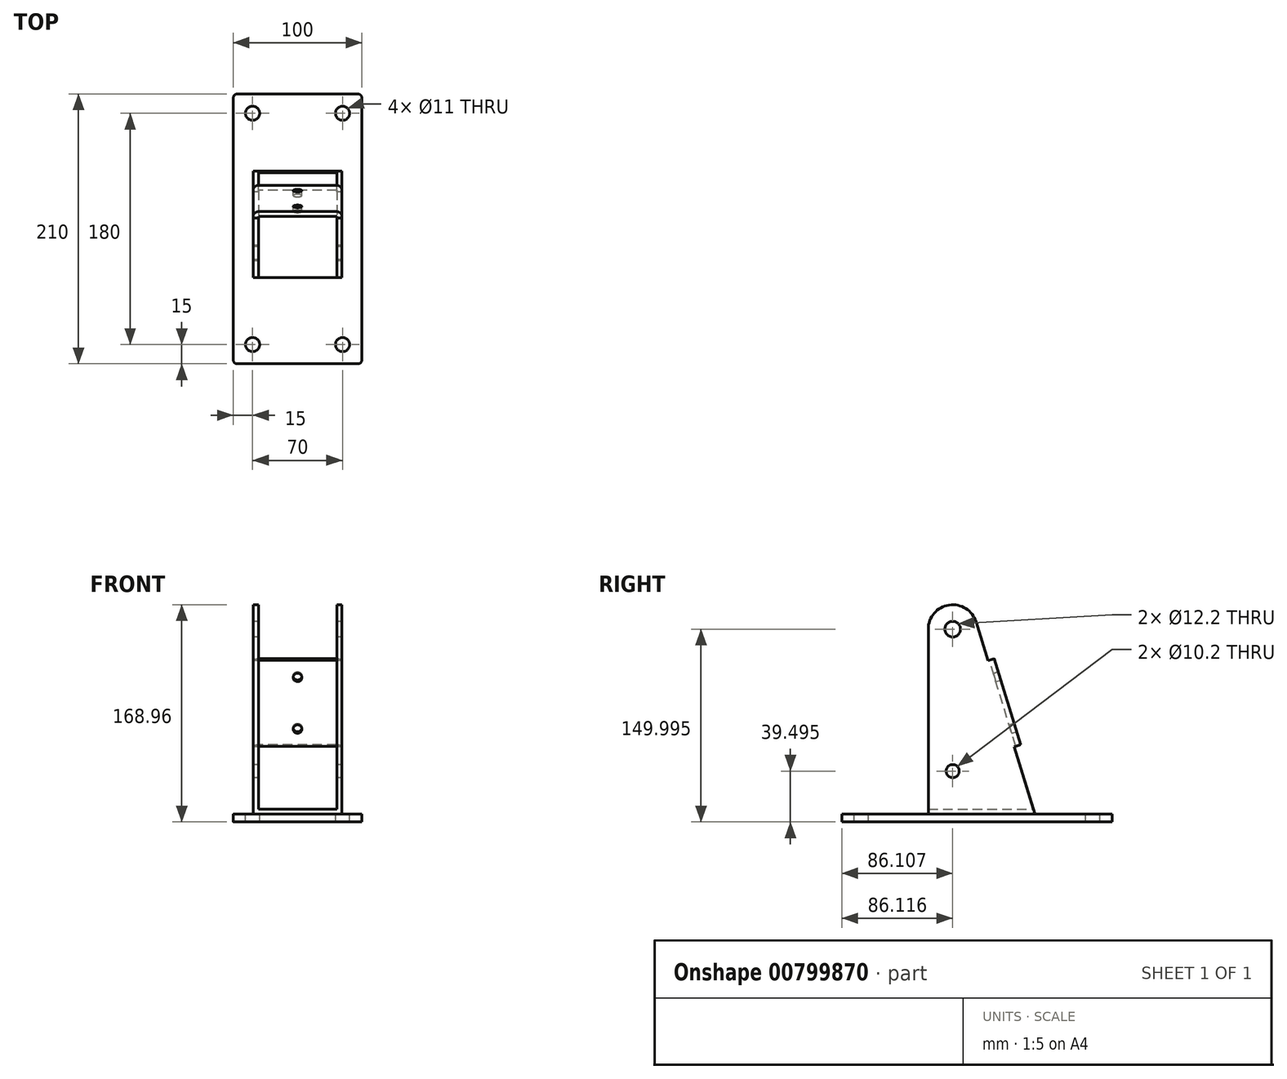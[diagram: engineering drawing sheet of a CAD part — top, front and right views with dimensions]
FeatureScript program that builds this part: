
annotation { "Feature Type Name" : "Feature", "Feature Type Description" : "" }
export const myFeature = defineFeature(function(context is Context, id is Id, definition is map)
    precondition{}
    {
        {
            var Q0;
            Q0=qCreatedBy(makeId("Right.planeOp"),FACE);
            var sketch = newSketch(context, id + "F0", { "sketchPlane" : qUnion([Q0])});
            skLineSegment(sketch, "E0", {"start": v(105, -84.48) * mm, "end": v(-105, -84.48) * mm});
            skLineSegment(sketch, "E1", {"start": v(-105, -84.48) * mm, "end": v(-105, -78.48) * mm});
            skLineSegment(sketch, "E2", {"start": v(-105, -78.48) * mm, "end": v(105, -78.48) * mm});
            skLineSegment(sketch, "E3", {"start": v(105, -78.48) * mm, "end": v(105, -84.48) * mm});
            skLineSegment(sketch, "E4", {"start": v(-37.88, -78.48) * mm, "end": v(45, -78.48) * mm});
            skLineSegment(sketch, "E5", {"start": v(-37.88, 65.48) * mm, "end": v(-37.88, -78.48) * mm});
            skLineSegment(sketch, "E6", {"start": v(28.94, -25.97) * mm, "end": v(45, -78.48) * mm});
            skLineSegment(sketch, "E7", {"start": v(1.89, -78.48) * mm, "end": v(-3.77, -78.48) * mm});
            skCircle(sketch, "E8", {"center": v(-18.88, -44.98) * mm, "radius": 5.1 * mm});
            skCircle(sketch, "E9", {"center": v(-18.9, 65.52) * mm, "radius": 6.1 * mm});
            skArc(sketch, "E10", {"start": v(-0.71, 71.04) * mm, "mid": v(-21.7, 84.28) * mm, "end": v(-37.88, 65.48) * mm});
            skLineSegment(sketch, "E11", {"start": v(-0.71, 71.04) * mm, "end": v(8.48, 40.97) * mm});
            skLineSegment(sketch, "E12", {"start": v(13.45, 42.5) * mm, "end": v(8.48, 40.97) * mm});
            skLineSegment(sketch, "E13", {"start": v(13.45, 42.5) * mm, "end": v(33.92, -24.45) * mm});
            skLineSegment(sketch, "E14", {"start": v(33.92, -24.45) * mm, "end": v(28.94, -25.97) * mm});
            skSolve(sketch);
        }
        {
            var Q0;
            {var subQ1=sQuery(id+"F0.wireOp",EDGE,"E5");Q0=makeQuery(id+"F0.imprint","IMPRINT",FACE,{"disambiguationData":[TD([[makeQuery(id+"F0.imprint","IMPRINT",EDGE,{"derivedFrom":subQ1}),1.0]])]});}
            extrude(context, id + "F1", {"entities" : qUnion([Q0]), "endBound" : BoundingType.SYMMETRIC, "depth" : 69 * mm, "offsetDistance" : 25 * mm});
        }
        {
            var Q0;
            Q0=makeQuery(id+"F1.opExtrude","CAP_EDGE",EDGE,{"disambiguationData":[OSD([sQuery(id+"F0.wireOp",EDGE,"E13")])],"isStart":true});
            var Q1;
            Q1=makeQuery(id+"F1.opExtrude","CAP_EDGE",EDGE,{"disambiguationData":[OSD([sQuery(id+"F0.wireOp",EDGE,"E13")])],"isStart":false});
            fillet(context, id + "F2", {"entities" : qUnion([Q0, Q1]), "radius" : 4 * mm, "tangentPropagation" : true, "allowEdgeOverflow" : false});
        }
        {
            var Q0;
            Q0=makeQuery(id+"F1.opExtrude","SWEPT_FACE",FACE,{"disambiguationData":[OSD([sQuery(id+"F0.wireOp",EDGE,"E5")])]});
            var Q1;
            Q1=makeQuery(id+"F1.opExtrude","SWEPT_FACE",FACE,{"disambiguationData":[OSD([sQuery(id+"F0.wireOp",EDGE,"E10")])]});
            var Q2;
            Q2=makeQuery(id+"F1.opExtrude","SWEPT_FACE",FACE,{"disambiguationData":[OSD([sQuery(id+"F0.wireOp",EDGE,"E11")])]});
            var Q3;
            Q3=makeQuery(id+"F1.opExtrude","SWEPT_FACE",FACE,{"disambiguationData":[OSD([sQuery(id+"F0.wireOp",EDGE,"E6")])]});
            var Q4;
            Q4=makeQuery(id+"F4.opExtrude","SWEPT_FACE",FACE,{"disambiguationData":[OSD([sQuery(id+"F0.wireOp",EDGE,"E0")])]});
            var Q5;
            Q5=makeQuery(id+"F1.opExtrude","SWEPT_FACE",FACE,{"disambiguationData":[OSD([sQuery(id+"F0.wireOp",EDGE,"E12")])]});
            var Q6;
            Q6=makeQuery(id+"F1.opExtrude","SWEPT_FACE",FACE,{"disambiguationData":[OSD([sQuery(id+"F0.wireOp",EDGE,"E14")])]});
            var Q7;
            Q7=makeQuery(id+"F1.opExtrude","SWEPT_FACE",FACE,{"disambiguationData":[OSD([sQuery(id+"F0.wireOp",EDGE,"E4"),sQuery(id+"F0.wireOp",EDGE,"E7")])]});
            var Q8;
            Q8=makeQuery(id+"F1.opExtrude","SWEPT_FACE",FACE,{"disambiguationData":[OSD([sQuery(id+"F0.wireOp",EDGE,"E9")])]});
            var Q9;
            Q9=makeQuery(id+"F1.opExtrude","SWEPT_FACE",FACE,{"disambiguationData":[OSD([sQuery(id+"F0.wireOp",EDGE,"E8")])]});
            shell(context, id + "F3", {"entities" : qUnion([Q0, Q1, Q2, Q3, Q4, Q5, Q6, Q7, Q8, Q9]), "thickness" : 4 * mm});
        }
        {
            var Q0;
            Q0=makeQuery(id+"F0.imprint","IMPRINT",FACE,{"disambiguationData":[TD([[makeQuery(id+"F0.imprint","IMPRINT",EDGE,{"derivedFrom":sQuery(id+"F0.wireOp",EDGE,"E0")}),-1.0]])]});
            extrude(context, id + "F4", {"entities" : qUnion([Q0]), "depth" : 50 * mm, "offsetDistance" : 25 * mm, "hasSecondDirection" : true, "secondDirectionOppositeDirection" : true, "secondDirectionDepth" : 50 * mm});
        }
        {
            var Q0;
            Q0=makeQuery(id+"F4.opExtrude","CAP_EDGE",EDGE,{"disambiguationData":[OSD([sQuery(id+"F0.wireOp",EDGE,"E1")])],"isStart":true});
            var Q1;
            Q1=makeQuery(id+"F4.opExtrude","CAP_EDGE",EDGE,{"disambiguationData":[OSD([sQuery(id+"F0.wireOp",EDGE,"E1")])],"isStart":false});
            var Q2;
            Q2=makeQuery(id+"F4.opExtrude","CAP_EDGE",EDGE,{"disambiguationData":[OSD([sQuery(id+"F0.wireOp",EDGE,"E3")])],"isStart":false});
            var Q3;
            Q3=makeQuery(id+"F4.opExtrude","CAP_EDGE",EDGE,{"disambiguationData":[OSD([sQuery(id+"F0.wireOp",EDGE,"E3")])],"isStart":true});
            fillet(context, id + "F5", {"entities" : qUnion([Q0, Q1, Q2, Q3]), "radius" : 3 * mm, "tangentPropagation" : true, "allowEdgeOverflow" : false});
        }
        {
            var Q0;
            Q0=makeQuery(id+"F4.opExtrude","SWEPT_FACE",FACE,{"disambiguationData":[OSD([sQuery(id+"F0.wireOp",EDGE,"E2"),sQuery(id+"F0.wireOp",EDGE,"E4"),sQuery(id+"F0.wireOp",EDGE,"E7")])]});
            var sketch = newSketch(context, id + "F6", { "sketchPlane" : qUnion([Q0])});
            skPoint(sketch, "E15", {"position": v(-35, -90) * mm});
            skPoint(sketch, "E16.0.1.0", {"position": v(-35, 90) * mm});
            skPoint(sketch, "E16.1.0.0", {"position": v(35, -90) * mm});
            skPoint(sketch, "E16.1.1.0", {"position": v(35, 90) * mm});
            skLineSegment(sketch, "E16.direction1", {"start": v(-35, -90) * mm, "end": v(35, -90) * mm, "construction": true});
            skLineSegment(sketch, "E16.direction2", {"start": v(-35, -90) * mm, "end": v(-35, 90) * mm, "construction": true});
            skSolve(sketch);
        }
        {
            var Q0;
            Q0=sQuery(id+"F6.wireOp",VERTEX,"E16.0.1.0");
            var Q1;
            Q1=sQuery(id+"F6.wireOp",VERTEX,"E15");
            var Q2;
            Q2=sQuery(id+"F6.wireOp",VERTEX,"E16.1.0.0");
            var Q3;
            Q3=sQuery(id+"F6.wireOp",VERTEX,"E16.1.1.0");
            var Q4;
            Q4=makeQuery(id+"F4.opExtrude","SWEPT_BODY",BODY,{"disambiguationData":[OSD([sQuery(id+"F0.wireOp",EDGE,"E0"),sQuery(id+"F0.wireOp",EDGE,"E1"),sQuery(id+"F0.wireOp",EDGE,"E2"),sQuery(id+"F0.wireOp",EDGE,"E3"),sQuery(id+"F0.wireOp",EDGE,"E4"),sQuery(id+"F0.wireOp",EDGE,"E7")])]});
            hole(context, id + "F7", {"style" : HoleStyle.SIMPLE, "endStyle" : HoleEndStyle.THROUGH, "standardTappedOrClearance" : lookupTablePath({ "standard" : "ISO", "size" : "11", "type" : "Drilled" }), "standardBlindInLast" : lookupTablePath({ "standard" : "ISO", "size" : "11", "type" : "Drilled" }), "holeDiameter" : 11 * mm, "majorDiameter" : 5 * mm, "isTappedThrough" : true, "tappedDepth" : 12 * mm, "tapClearance" : 3, "startFromSketch" : true, "locations" : qUnion([Q0, Q1, Q2, Q3]), "scope" : qUnion([Q4])});
        }
        {
            var Q0;
            Q0=makeQuery(id+"F1.opExtrude","SWEPT_FACE",FACE,{"disambiguationData":[OSD([sQuery(id+"F0.wireOp",EDGE,"E13")])]});
            var sketch = newSketch(context, id + "F8", { "sketchPlane" : qUnion([Q0])});
            skPoint(sketch, "E17", {"position": v(0, 22.7) * mm});
            skPoint(sketch, "E18", {"position": v(0, -19.3) * mm});
            skSolve(sketch);
        }
        {
            var Q0;
            Q0=sQuery(id+"F8.wireOp",VERTEX,"E17");
            var Q1;
            Q1=sQuery(id+"F8.wireOp",VERTEX,"E18");
            var Q2;
            Q2=makeQuery(id+"F1.opExtrude","SWEPT_BODY",BODY,{"disambiguationData":[OSD([sQuery(id+"F0.wireOp",EDGE,"E4"),sQuery(id+"F0.wireOp",EDGE,"E5"),sQuery(id+"F0.wireOp",EDGE,"E6"),sQuery(id+"F0.wireOp",EDGE,"E7"),sQuery(id+"F0.wireOp",EDGE,"E8"),sQuery(id+"F0.wireOp",EDGE,"E9"),sQuery(id+"F0.wireOp",EDGE,"E10"),sQuery(id+"F0.wireOp",EDGE,"E11"),sQuery(id+"F0.wireOp",EDGE,"E12"),sQuery(id+"F0.wireOp",EDGE,"E13"),sQuery(id+"F0.wireOp",EDGE,"E14")])]});
            hole(context, id + "F9", {"style" : HoleStyle.SIMPLE, "endStyle" : HoleEndStyle.THROUGH, "standardTappedOrClearance" : lookupTablePath({ "standard" : "ISO", "size" : "6.8", "type" : "Drilled" }), "standardBlindInLast" : lookupTablePath({ "standard" : "ISO", "size" : "6.8", "type" : "Drilled" }), "holeDiameter" : 6.8 * mm, "majorDiameter" : 5 * mm, "isTappedThrough" : true, "tappedDepth" : 12 * mm, "tapClearance" : 3, "startFromSketch" : true, "locations" : qUnion([Q0, Q1]), "scope" : qUnion([Q2])});
        }
    });
